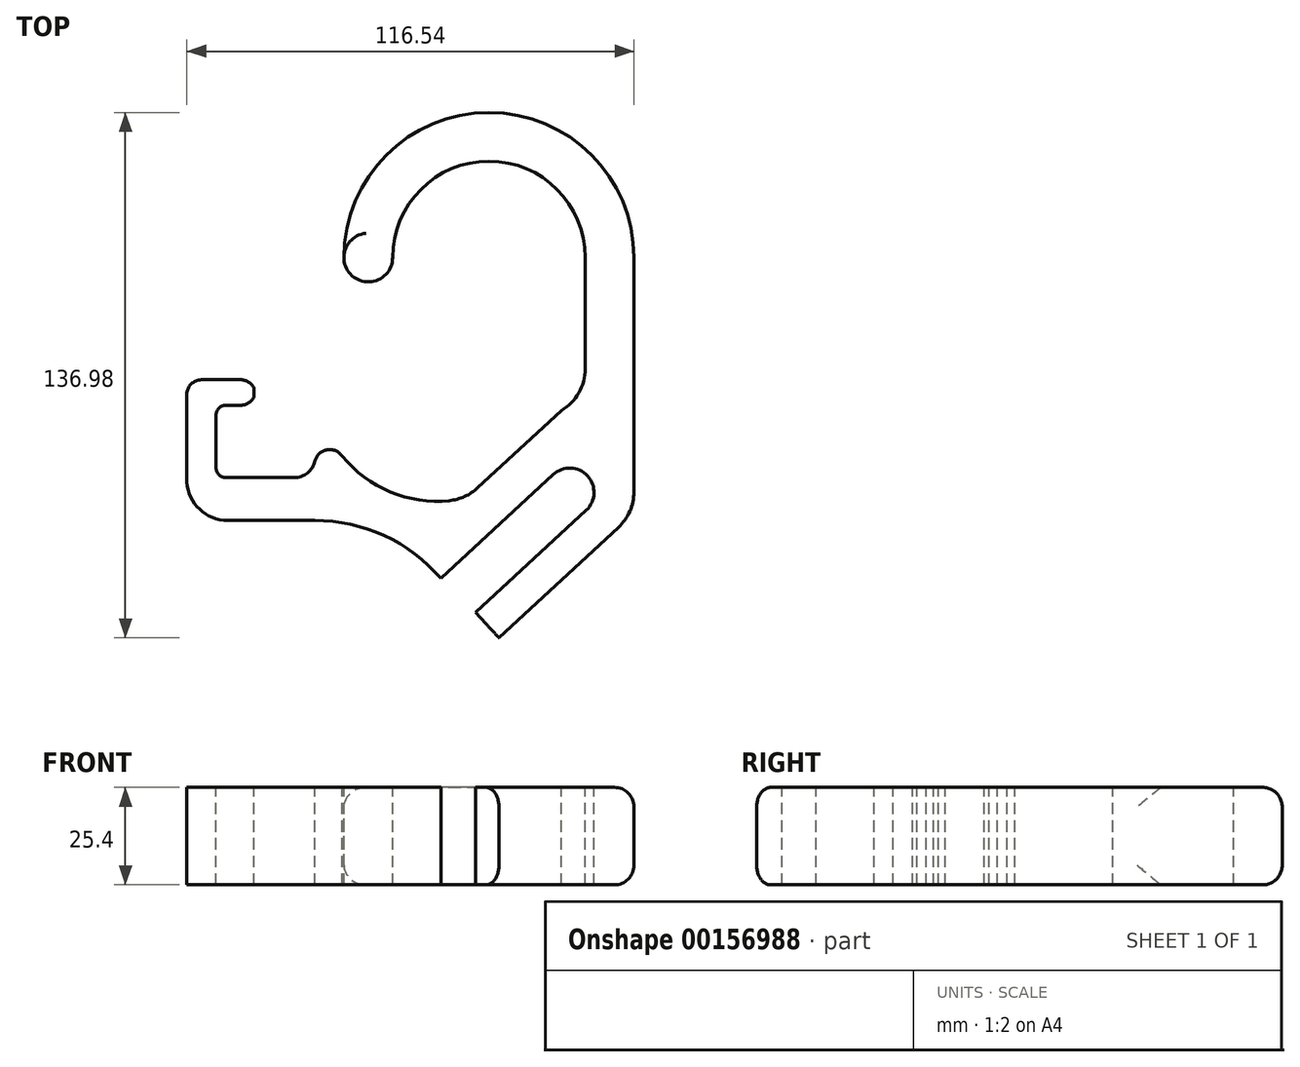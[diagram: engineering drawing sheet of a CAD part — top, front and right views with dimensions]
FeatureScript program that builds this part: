
annotation { "Feature Type Name" : "Feature", "Feature Type Description" : "" }
export const myFeature = defineFeature(function(context is Context, id is Id, definition is map)
    precondition{}
    {
        {
            var Q0;
            Q0=qCreatedBy(makeId("Top.planeOp"),FACE);
            var sketch = newSketch(context, id + "F0", { "sketchPlane" : qUnion([Q0])});
            skLineSegment(sketch, "E0", {"start": v(62.2, 44.55) * mm, "end": v(62.2, -16.55) * mm});
            skLineSegment(sketch, "E1", {"start": v(11.87, -39.16) * mm, "end": v(41.16, -12.06) * mm});
            skLineSegment(sketch, "E2", {"start": v(49.77, -21.36) * mm, "end": v(20.94, -48.04) * mm});
            skLineSegment(sketch, "E3", {"start": v(20.94, -48.04) * mm, "end": v(27.04, -54.64) * mm});
            skLineSegment(sketch, "E4", {"start": v(-54.33, 8.84) * mm, "end": v(-54.33, -14.02) * mm});
            skLineSegment(sketch, "E5", {"start": v(-43.71, -24.02) * mm, "end": v(-21.01, -24.02) * mm});
            skArc(sketch, "E6", {"start": v(-13.84, -7.3) * mm, "mid": v(-1.31, -16.6) * mm, "end": v(14.13, -18.86) * mm});
            skLineSegment(sketch, "E7", {"start": v(-46.71, 3.46) * mm, "end": v(-46.71, -10.33) * mm});
            skLineSegment(sketch, "E8", {"start": v(-50.52, 12.65) * mm, "end": v(-40.34, 12.65) * mm});
            skArc(sketch, "E9", {"start": v(-54.33, -14.02) * mm, "mid": v(-51, -21.12) * mm, "end": v(-43.71, -24.02) * mm});
            skArc(sketch, "E10", {"start": v(-26.4, -12.87) * mm, "mid": v(-22.9, -11.65) * mm, "end": v(-20.95, -8.5) * mm});
            skLineSegment(sketch, "E11", {"start": v(-44.17, -12.87) * mm, "end": v(-26.4, -12.87) * mm});
            skArc(sketch, "E12", {"start": v(11.87, -39.16) * mm, "mid": v(-2.91, -27.99) * mm, "end": v(-21.01, -24.02) * mm});
            skLineSegment(sketch, "E13", {"start": v(49.5, 15.56) * mm, "end": v(49.5, 44.55) * mm});
            skArc(sketch, "E14", {"start": v(49.5, 44.55) * mm, "mid": v(24.41, 69.64) * mm, "end": v(-0.69, 44.55) * mm});
            skArc(sketch, "E15", {"start": v(62.2, 44.55) * mm, "mid": v(24.41, 82.34) * mm, "end": v(-13.39, 44.55) * mm});
            skPoint(sketch, "E16.visualSharp", {"position": v(49.5, 7.25) * mm});
            skArc(sketch, "E16.filletArc", {"start": v(43.25, 4.62) * mm, "mid": v(47.83, 9.26) * mm, "end": v(49.5, 15.56) * mm});
            skPoint(sketch, "E17.visualSharp", {"position": v(-22.31, -3.53) * mm});
            skArc(sketch, "E18", {"start": v(-13.84, -7.3) * mm, "mid": v(-17.78, -5.6) * mm, "end": v(-20.95, -8.5) * mm});
            skLineSegment(sketch, "E19", {"start": v(27.04, -54.64) * mm, "end": v(58.13, -25.87) * mm});
            skPoint(sketch, "E20.visualSharp", {"position": v(62.2, -22.1) * mm});
            skArc(sketch, "E20.filletArc", {"start": v(58.13, -25.87) * mm, "mid": v(61.15, -21.64) * mm, "end": v(62.2, -16.55) * mm});
            skArc(sketch, "E21", {"start": v(49.77, -21.36) * mm, "mid": v(50.12, -12.4) * mm, "end": v(41.16, -12.06) * mm});
            skLineSegment(sketch, "E22", {"start": v(43.25, 4.62) * mm, "end": v(21.46, -15.54) * mm});
            skPoint(sketch, "E23.visualSharp", {"position": v(18.77, -18.03) * mm});
            skArc(sketch, "E23.filletArc", {"start": v(14.13, -18.86) * mm, "mid": v(18.06, -17.8) * mm, "end": v(21.46, -15.54) * mm});
            skLineSegment(sketch, "E24", {"start": v(-44.17, 6) * mm, "end": v(-40.34, 6) * mm});
            skPoint(sketch, "E25.visualSharp", {"position": v(-46.71, 6) * mm});
            skArc(sketch, "E25.filletArc", {"start": v(-44.17, 6) * mm, "mid": v(-45.97, 5.25) * mm, "end": v(-46.71, 3.46) * mm});
            skPoint(sketch, "E26.visualSharp", {"position": v(-46.71, -12.87) * mm});
            skArc(sketch, "E26.filletArc", {"start": v(-46.71, -10.33) * mm, "mid": v(-45.97, -12.13) * mm, "end": v(-44.17, -12.87) * mm});
            skArc(sketch, "E27", {"start": v(-36.9, 10.6) * mm, "mid": v(-38.33, 12.1) * mm, "end": v(-40.34, 12.65) * mm});
            skArc(sketch, "E28", {"start": v(-40.34, 6) * mm, "mid": v(-38.33, 6.55) * mm, "end": v(-36.9, 8.05) * mm});
            skLineSegment(sketch, "E29", {"start": v(-36.9, 10.6) * mm, "end": v(-36.9, 8.05) * mm});
            skPoint(sketch, "E30.visualSharp", {"position": v(-54.33, 12.65) * mm});
            skArc(sketch, "E30.filletArc", {"start": v(-50.52, 12.65) * mm, "mid": v(-53.22, 11.53) * mm, "end": v(-54.33, 8.84) * mm});
            skLineSegment(sketch, "E31", {"start": v(-13.39, 44.55) * mm, "end": v(-0.69, 44.55) * mm});
            skLineSegment(sketch, "E32", {"start": v(49.5, 44.55) * mm, "end": v(62.2, 44.55) * mm});
            skArc(sketch, "E33", {"start": v(-13.39, 44.55) * mm, "mid": v(-7.04, 38.18) * mm, "end": v(-0.69, 44.55) * mm});
            skSolve(sketch);
        }
        {
            var Q0;
            Q0=makeQuery(id+"F0.imprint","IMPRINT",FACE,{"disambiguationData":[TD([[makeQuery(id+"F0.imprint","IMPRINT",EDGE,{"derivedFrom":sQuery(id+"F0.wireOp",EDGE,"E0")}),-1.0]])]});
            var Q1;
            {var subQ0=sQuery(id+"F0.wireOp",EDGE,"E8");Q1=makeQuery(id+"F0.imprint","IMPRINT",FACE,{"disambiguationData":[TD([[makeQuery(id+"F0.imprint","IMPRINT",EDGE,{"derivedFrom":subQ0}),-1.0]])]});}
            var Q2;
            Q2=makeQuery(id+"F0.imprint","IMPRINT",FACE,{"disambiguationData":[TD([[makeQuery(id+"F0.imprint","IMPRINT",EDGE,{"derivedFrom":sQuery(id+"F0.wireOp",EDGE,"E14")}),-1.0]])]});
            var Q3;
            Q3=makeQuery(id+"F0.imprint","IMPRINT",FACE,{"disambiguationData":[TD([[makeQuery(id+"F0.imprint","IMPRINT",EDGE,{"derivedFrom":sQuery(id+"F0.wireOp",EDGE,"E31")}),-1.0]])]});
            extrude(context, id + "F1", {"entities" : qUnion([Q0, Q1, Q2, Q3]), "oppositeDirection" : true, "depth" : 25.4 * mm});
        }
        {
            var Q0;
            Q0=makeQuery(id+"F1.opExtrude","CAP_EDGE",EDGE,{"disambiguationData":[OSD([sQuery(id+"F0.wireOp",EDGE,"E15")])],"isStart":false});
            var Q1;
            Q1=makeQuery(id+"F1.opExtrude","CAP_EDGE",EDGE,{"disambiguationData":[OSD([sQuery(id+"F0.wireOp",EDGE,"E15")])],"isStart":true});
            fillet(context, id + "F2", {"entities" : qUnion([Q0, Q1]), "radius" : 5.08 * mm, "tangentPropagation" : true, "allowEdgeOverflow" : false});
        }
    });
